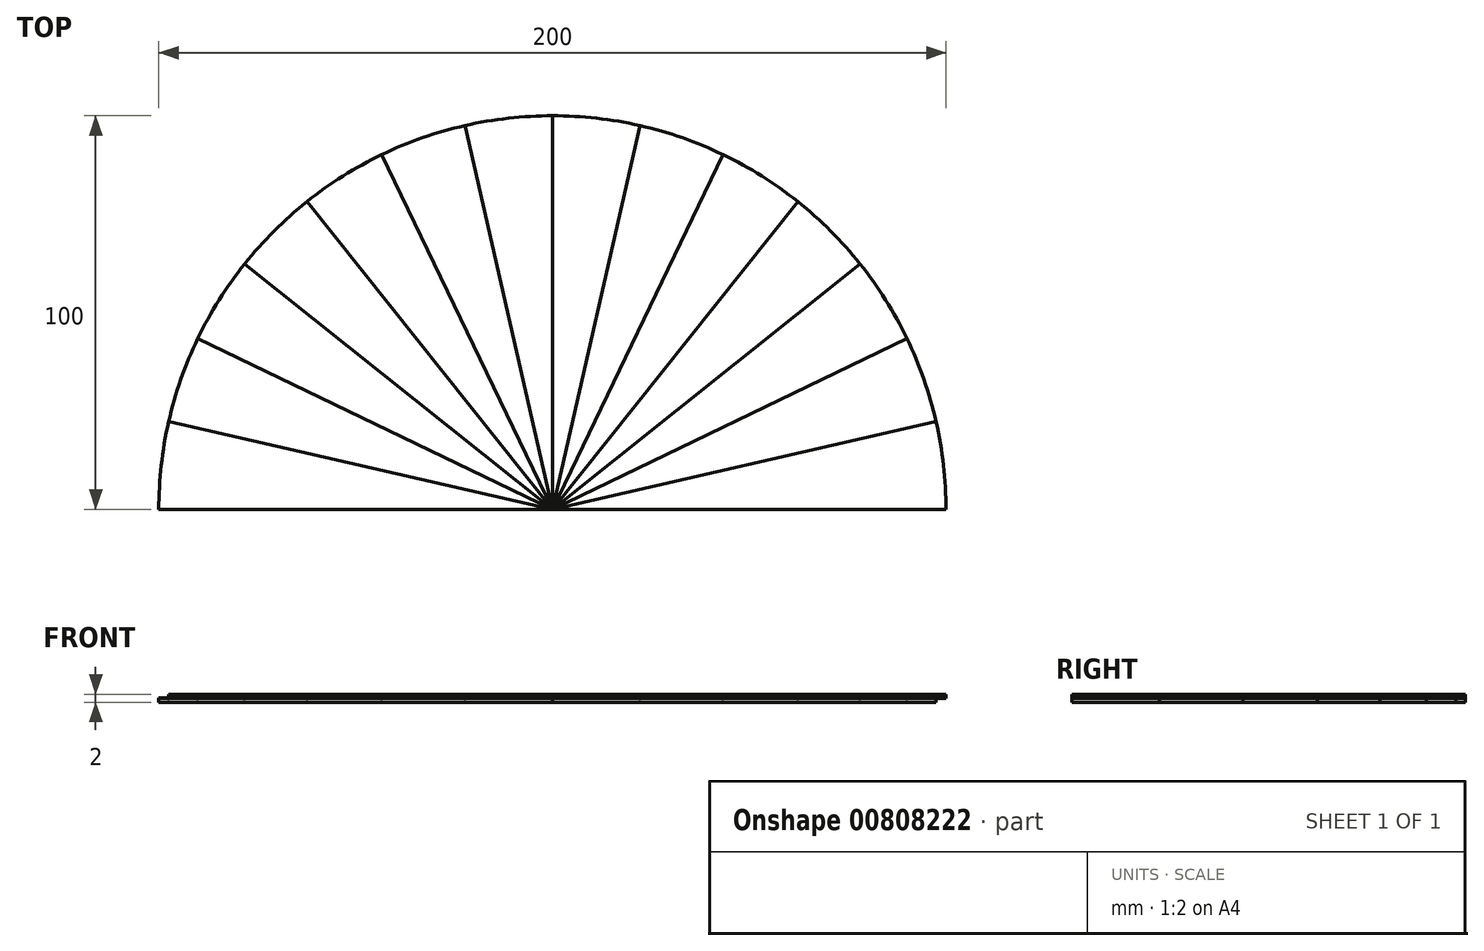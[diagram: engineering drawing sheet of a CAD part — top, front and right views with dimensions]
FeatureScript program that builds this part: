
annotation { "Feature Type Name" : "Feature", "Feature Type Description" : "" }
export const myFeature = defineFeature(function(context is Context, id is Id, definition is map)
    precondition{}
    {
        {
            var Q0;
            Q0=qCreatedBy(makeId("Top.planeOp"),FACE);
            var sketch = newSketch(context, id + "F0", { "sketchPlane" : qUnion([Q0])});
            skLineSegment(sketch, "E0", {"start": v(0, 0) * mm, "end": v(100, 0) * mm});
            skLineSegment(sketch, "E1", {"start": v(0, 0) * mm, "end": v(-100, 0) * mm});
            skArc(sketch, "E2", {"start": v(100, 0) * mm, "mid": v(0, 100) * mm, "end": v(-100, 0) * mm});
            skLineSegment(sketch, "E3.1.0", {"start": v(0, 0) * mm, "end": v(-97.5, 22.25) * mm});
            skLineSegment(sketch, "E3.2.0", {"start": v(0, 0) * mm, "end": v(-90.1, 43.39) * mm});
            skLineSegment(sketch, "E3.3.0", {"start": v(0, 0) * mm, "end": v(-78.18, 62.35) * mm});
            skLineSegment(sketch, "E3.4.0", {"start": v(0, 0) * mm, "end": v(-62.35, 78.18) * mm});
            skLineSegment(sketch, "E3.5.0", {"start": v(0, 0) * mm, "end": v(-43.39, 90.1) * mm});
            skLineSegment(sketch, "E3.6.0", {"start": v(0, 0) * mm, "end": v(-22.25, 97.5) * mm});
            skLineSegment(sketch, "E3.7.0", {"start": v(0, 0) * mm, "end": v(0, 100) * mm});
            skLineSegment(sketch, "E3.8.0", {"start": v(0, 0) * mm, "end": v(22.25, 97.5) * mm});
            skLineSegment(sketch, "E3.9.0", {"start": v(0, 0) * mm, "end": v(43.39, 90.1) * mm});
            skLineSegment(sketch, "E3.10.0", {"start": v(0, 0) * mm, "end": v(62.35, 78.18) * mm});
            skLineSegment(sketch, "E3.11.0", {"start": v(0, 0) * mm, "end": v(78.18, 62.35) * mm});
            skLineSegment(sketch, "E3.12.0", {"start": v(0, 0) * mm, "end": v(90.1, 43.39) * mm});
            skLineSegment(sketch, "E3.13.0", {"start": v(0, 0) * mm, "end": v(97.5, 22.25) * mm});
            skLineSegment(sketch, "E3.anchor1", {"start": v(0, 0) * mm, "end": v(-100, 0) * mm, "construction": true});
            skLineSegment(sketch, "E3.anchor2", {"start": v(0, 0) * mm, "end": v(100, 0) * mm, "construction": true});
            skSolve(sketch);
        }
        {
            var Q0;
            Q0=qSketchRegion(id+"F0",true);
            extrude(context, id + "F1", {"entities" : qUnion([Q0]), "endBound" : BoundingType.SYMMETRIC, "depth" : 0.2 * mm, "offsetDistance" : 25 * mm});
        }
        {
            var Q0;
            {var subQ0=sQuery(id+"F0.wireOp",EDGE,"E1");Q0=makeQuery(id+"F0.imprint","IMPRINT",FACE,{"disambiguationData":[TD([[makeQuery(id+"F0.imprint","IMPRINT",EDGE,{"derivedFrom":subQ0}),-1.0]])]});}
            var Q1;
            {var subQ0=sQuery(id+"F0.wireOp",EDGE,"E3.2.0");Q1=makeQuery(id+"F0.imprint","IMPRINT",FACE,{"disambiguationData":[TD([[makeQuery(id+"F0.imprint","IMPRINT",EDGE,{"derivedFrom":subQ0}),-1.0]])]});}
            var Q2;
            {var subQ0=sQuery(id+"F0.wireOp",EDGE,"E3.4.0");Q2=makeQuery(id+"F0.imprint","IMPRINT",FACE,{"disambiguationData":[TD([[makeQuery(id+"F0.imprint","IMPRINT",EDGE,{"derivedFrom":subQ0}),-1.0]])]});}
            var Q3;
            {var subQ0=sQuery(id+"F0.wireOp",EDGE,"E3.6.0");Q3=makeQuery(id+"F0.imprint","IMPRINT",FACE,{"disambiguationData":[TD([[makeQuery(id+"F0.imprint","IMPRINT",EDGE,{"derivedFrom":subQ0}),-1.0]])]});}
            var Q4;
            {var subQ0=sQuery(id+"F0.wireOp",EDGE,"E3.8.0");Q4=makeQuery(id+"F0.imprint","IMPRINT",FACE,{"disambiguationData":[TD([[makeQuery(id+"F0.imprint","IMPRINT",EDGE,{"derivedFrom":subQ0}),-1.0]])]});}
            var Q5;
            {var subQ0=sQuery(id+"F0.wireOp",EDGE,"E3.10.0");Q5=makeQuery(id+"F0.imprint","IMPRINT",FACE,{"disambiguationData":[TD([[makeQuery(id+"F0.imprint","IMPRINT",EDGE,{"derivedFrom":subQ0}),-1.0]])]});}
            var Q6;
            {var subQ0=sQuery(id+"F0.wireOp",EDGE,"E3.12.0");Q6=makeQuery(id+"F0.imprint","IMPRINT",FACE,{"disambiguationData":[TD([[makeQuery(id+"F0.imprint","IMPRINT",EDGE,{"derivedFrom":subQ0}),-1.0]])]});}
            extrude(context, id + "F2", {"entities" : qUnion([Q0, Q1, Q2, Q3, Q4, Q5, Q6]), "oppositeDirection" : true, "depth" : 1 * mm, "offsetDistance" : 25 * mm});
        }
        {
            var Q0;
            {var subQ0=sQuery(id+"F0.wireOp",EDGE,"E3.1.0");Q0=makeQuery(id+"F0.imprint","IMPRINT",FACE,{"disambiguationData":[TD([[makeQuery(id+"F0.imprint","IMPRINT",EDGE,{"derivedFrom":subQ0}),-1.0]])]});}
            var Q1;
            {var subQ0=sQuery(id+"F0.wireOp",EDGE,"E3.3.0");Q1=makeQuery(id+"F0.imprint","IMPRINT",FACE,{"disambiguationData":[TD([[makeQuery(id+"F0.imprint","IMPRINT",EDGE,{"derivedFrom":subQ0}),-1.0]])]});}
            var Q2;
            {var subQ0=sQuery(id+"F0.wireOp",EDGE,"E3.5.0");Q2=makeQuery(id+"F0.imprint","IMPRINT",FACE,{"disambiguationData":[TD([[makeQuery(id+"F0.imprint","IMPRINT",EDGE,{"derivedFrom":subQ0}),-1.0]])]});}
            var Q3;
            {var subQ0=sQuery(id+"F0.wireOp",EDGE,"E3.7.0");Q3=makeQuery(id+"F0.imprint","IMPRINT",FACE,{"disambiguationData":[TD([[makeQuery(id+"F0.imprint","IMPRINT",EDGE,{"derivedFrom":subQ0}),-1.0]])]});}
            var Q4;
            {var subQ0=sQuery(id+"F0.wireOp",EDGE,"E3.9.0");Q4=makeQuery(id+"F0.imprint","IMPRINT",FACE,{"disambiguationData":[TD([[makeQuery(id+"F0.imprint","IMPRINT",EDGE,{"derivedFrom":subQ0}),-1.0]])]});}
            var Q5;
            {var subQ0=sQuery(id+"F0.wireOp",EDGE,"E3.11.0");Q5=makeQuery(id+"F0.imprint","IMPRINT",FACE,{"disambiguationData":[TD([[makeQuery(id+"F0.imprint","IMPRINT",EDGE,{"derivedFrom":subQ0}),-1.0]])]});}
            var Q6;
            {var subQ2=sQuery(id+"F0.wireOp",EDGE,"E3.13.0");Q6=makeQuery(id+"F0.imprint","IMPRINT",FACE,{"disambiguationData":[TD([[makeQuery(id+"F0.imprint","IMPRINT",EDGE,{"derivedFrom":subQ2}),-1.0]])]});}
            extrude(context, id + "F3", {"entities" : qUnion([Q0, Q1, Q2, Q3, Q4, Q5, Q6]), "depth" : 1 * mm, "offsetDistance" : 25 * mm});
        }
    });
